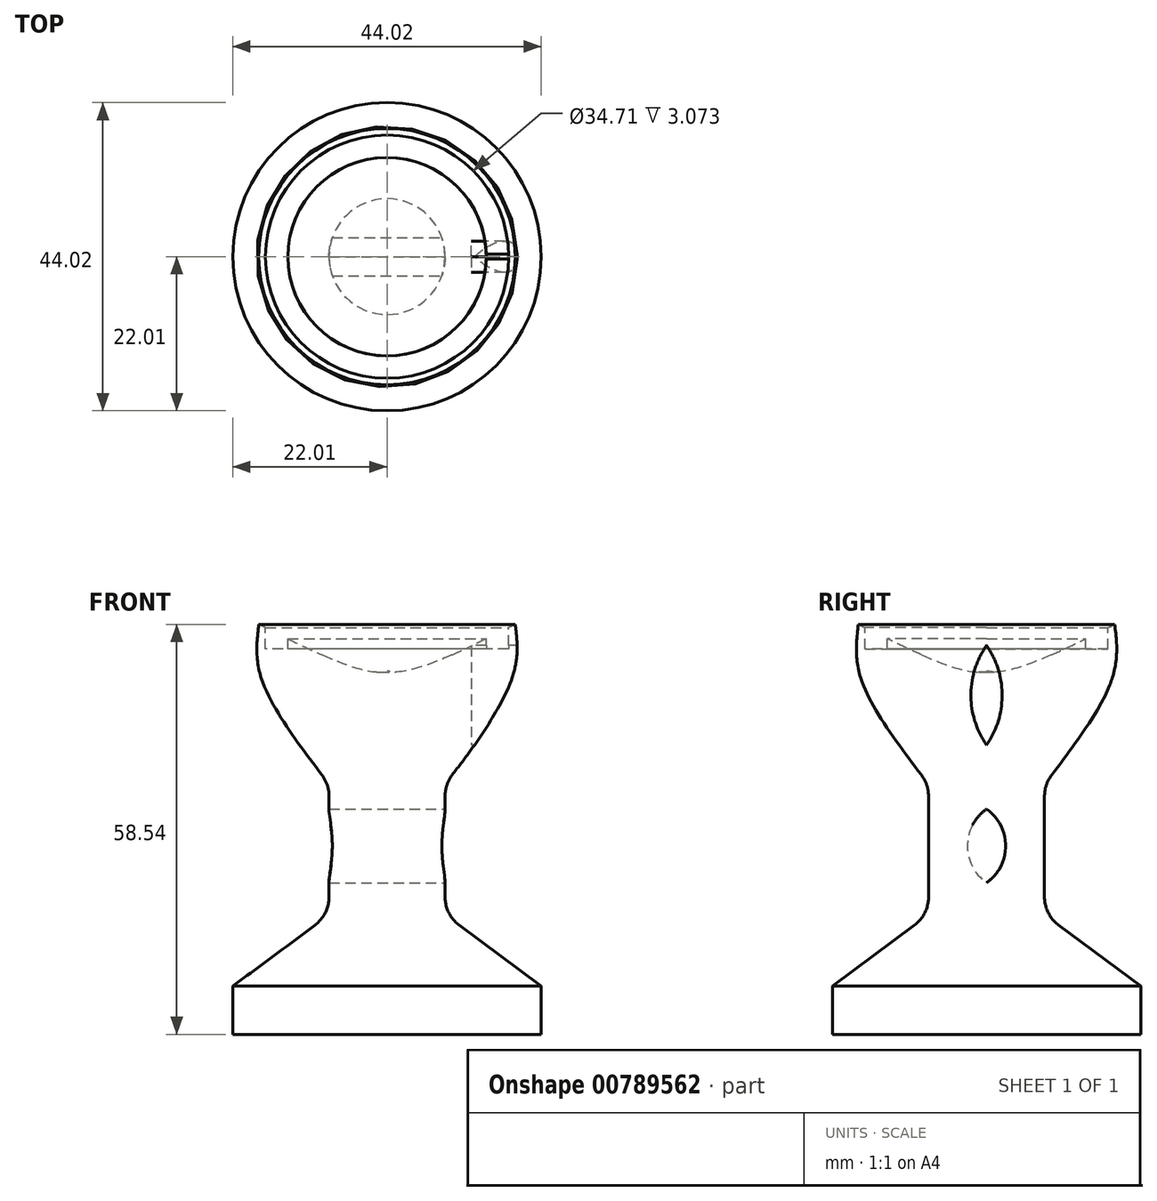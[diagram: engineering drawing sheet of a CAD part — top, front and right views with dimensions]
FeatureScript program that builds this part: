
annotation { "Feature Type Name" : "Feature", "Feature Type Description" : "" }
export const myFeature = defineFeature(function(context is Context, id is Id, definition is map)
    precondition{}
    {
        {
            var Q0;
            Q0=qCreatedBy(makeId("Front.planeOp"),FACE);
            var sketch = newSketch(context, id + "F0", { "sketchPlane" : qUnion([Q0])});
            skLineSegment(sketch, "E0.bottom", {"start": v(0, 0) * mm, "end": v(22, 0) * mm});
            skLineSegment(sketch, "E0.left", {"start": v(0, 0) * mm, "end": v(0, 13.74) * mm});
            skLineSegment(sketch, "E0.right", {"start": v(22, 0) * mm, "end": v(22, 6.87) * mm});
            skLineSegment(sketch, "E1.left", {"start": v(0, 13.74) * mm, "end": v(0, 52.15) * mm});
            skLineSegment(sketch, "E2.right", {"start": v(18.3, 58.54) * mm, "end": v(18.3, 58.54) * mm});
            skLineSegment(sketch, "E3", {"start": v(8.28, 35.7) * mm, "end": v(8.28, 17.11) * mm});
            skFitSpline(sketch, "E4", {"points": [v(17.98, 50.98) * mm, v(18.3, 58.54) * mm, v(0, 61.2) * mm], "startDerivative": vector(144.22, 129.07) * mm, "endDerivative": vector(29.63, 72.83) * mm});
            skLineSegment(sketch, "E5", {"start": v(0, 70) * mm, "end": v(0, 70) * mm});
            skLineSegment(sketch, "E6", {"start": v(0, 52.15) * mm, "end": v(0, 72.8) * mm});
            skArc(sketch, "E7", {"start": v(9.25, 54.18) * mm, "mid": v(10.84, 65.33) * mm, "end": v(2.23, 72.59) * mm});
            skLineSegment(sketch, "E8", {"start": v(8.28, 17.11) * mm, "end": v(22, 6.87) * mm});
            skFitSpline(sketch, "E9", {"points": [v(18.3, 58.54) * mm, v(17.98, 50.98) * mm, v(8.28, 35.7) * mm], "startDerivative": vector(2.18, -18.1) * mm, "endDerivative": vector(-20.6, -26.96) * mm});
            skArc(sketch, "E10", {"start": v(2.23, 72.59) * mm, "mid": v(4.72, 78.05) * mm, "end": v(0, 81.76) * mm});
            skLineSegment(sketch, "E11", {"start": v(0, 72.8) * mm, "end": v(0, 81.76) * mm});
            skSolve(sketch);
        }
        {
            var Q0;
            {var subQ0=sQuery(id+"F0.wireOp",EDGE,"E6");var subQ1=sQuery(id+"F0.wireOp",EDGE,"E5");var subQ2=makeQuery(id+"F0.imprint","INTERSECT",VERTEX,{"disambiguationData":[OD(0.0)],"derivedFrom":[subQ1,subQ0]});Q0=makeQuery(id+"F0.imprint","IMPRINT",FACE,{"disambiguationData":[TD([[makeQuery(id+"F0.imprint","IMPRINT",EDGE,{"disambiguationData":[TD([[subQ2,-1.0]])],"derivedFrom":subQ1}),1.0]])]});}
            var Q1;
            Q1=makeQuery(id+"F0.imprint","IMPRINT",FACE,{"disambiguationData":[TD([[makeQuery(id+"F0.imprint","IMPRINT",EDGE,{"derivedFrom":sQuery(id+"F0.wireOp",EDGE,"E0.bottom")}),1.0]])]});
            var Q2;
            Q2=sQuery(id+"F0.wireOp",EDGE,"E1.left");
            revolve(context, id + "F1", {"surfaceOperationType" : NewSurfaceOperationType.NEW, "entities" : qUnion([Q0, Q1]), "axis" : qUnion([Q2]), "revolveType" : RevolveType.FULL});
        }
        {
            var Q0;
            Q0=makeQuery(id+"F1.opRevolve","SWEPT_FACE",FACE,{"disambiguationData":[OSD([sQuery(id+"F0.wireOp",EDGE,"E3")])]});
            var Q1;
            Q1=makeQuery(id+"F1.opRevolve","SWEPT_EDGE",EDGE,{"disambiguationData":[OSD([sQuery(id+"F0.wireOp",EDGE,"iolcP0e3-W6rE-IeYN-R3CD-CLtWMC0POBNi"),sQuery(id+"F0.wireOp",EDGE,"E3")])]});
            var Q2;
            Q2=makeQuery(id+"F1.opRevolve","SWEPT_EDGE",EDGE,{"disambiguationData":[OSD([sQuery(id+"F0.wireOp",EDGE,"E3"),sQuery(id+"F0.wireOp",EDGE,"lH1SHDeB-0oN9-N9os-sk39-AU2wCfuFJ4HC")])]});
            fillet(context, id + "F2", {"entities" : qUnion([Q0, Q1, Q2]), "radius" : 5 * mm, "tangentPropagation" : true, "allowEdgeOverflow" : false});
        }
        {
            var Q0;
            Q0=qCreatedBy(makeId("Right.planeOp"),FACE);
            cPlane(context, id + "F3", {"entities" : qUnion([Q0]), "cplaneType" : CPlaneType.OFFSET, "offset" : 12 * mm, "width" : 150 * mm, "height" : 150 * mm});
        }
        {
            var Q0;
            Q0=qCreatedBy(id+"F3.planeOp",FACE);
            var sketch = newSketch(context, id + "F4", { "sketchPlane" : qUnion([Q0])});
            skArc(sketch, "E12", {"start": v(0, 21.65) * mm, "mid": v(2.73, 26.9) * mm, "end": v(0, 32.17) * mm});
            skArc(sketch, "E13.MirrorCS", {"start": v(0, 21.65) * mm, "mid": v(-2.73, 26.9) * mm, "end": v(0, 32.17) * mm});
            skSolve(sketch);
        }
        {
            var Q0;
            Q0 = qSketchRegion(id + "F4", true);
            extrude(context, id + "F5", {"entities" : qUnion([Q0]), "operationType" : NewBodyOperationType.REMOVE, "oppositeDirection" : true, "depth" : 25 * mm, "offsetDistance" : 25 * mm});
        }
        {
            var Q0;
            Q0=qCreatedBy(makeId("Top.planeOp"),FACE);
            cPlane(context, id + "F6", {"entities" : qUnion([Q0]), "cplaneType" : CPlaneType.OFFSET, "offset" : 70 * mm, "width" : 150 * mm, "height" : 150 * mm});
        }
        {
            var Q0;
            Q0=qCreatedBy(id+"F6.planeOp",FACE);
            var sketch = newSketch(context, id + "F7", { "sketchPlane" : qUnion([Q0])});
            skCircle(sketch, "E14", {"center": v(0, 0) * mm, "radius": 17.36 * mm});
            skCircle(sketch, "E15.0", {"center": v(0, 0) * mm, "radius": 14.16 * mm});
            skSolve(sketch);
        }
        {
            var Q0;
            Q0=makeQuery(id+"F7.imprint","IMPRINT",FACE,{"disambiguationData":[TD([[makeQuery(id+"F7.imprint","IMPRINT",EDGE,{"derivedFrom":sQuery(id+"F7.wireOp",EDGE,"E14")}),1.0]])]});
            extrude(context, id + "F8", {"entities" : qUnion([Q0]), "operationType" : NewBodyOperationType.REMOVE, "oppositeDirection" : true, "depth" : 15 * mm, "offsetDistance" : 25 * mm});
        }
        {
            var Q0;
            Q0=qCreatedBy(id+"F3.planeOp",FACE);
            var sketch = newSketch(context, id + "F9", { "sketchPlane" : qUnion([Q0])});
            skArc(sketch, "E16", {"start": v(0, 41.34) * mm, "mid": v(2.23, 48.43) * mm, "end": v(0, 55.53) * mm});
            skArc(sketch, "E17.MirrorCS", {"start": v(0, 41.34) * mm, "mid": v(-2.23, 48.43) * mm, "end": v(0, 55.53) * mm});
            skSolve(sketch);
        }
        {
            var Q0;
            Q0 = qSketchRegion(id + "F9", true);
            var Q1;
            Q1=sQuery(id+"F9.wireOp",EDGE,"E17.MirrorCS");
            var Q2;
            Q2=sQuery(id+"F9.wireOp",EDGE,"E16");
            extrude(context, id + "F10", {"entities" : qUnion([Q0]), "operationType" : NewBodyOperationType.REMOVE, "surfaceOperationType" : NewSurfaceOperationType.ADD, "surfaceEntities" : qUnion([Q1, Q2]), "depth" : 13.1 * mm, "offsetDistance" : 25 * mm});
        }
    });
